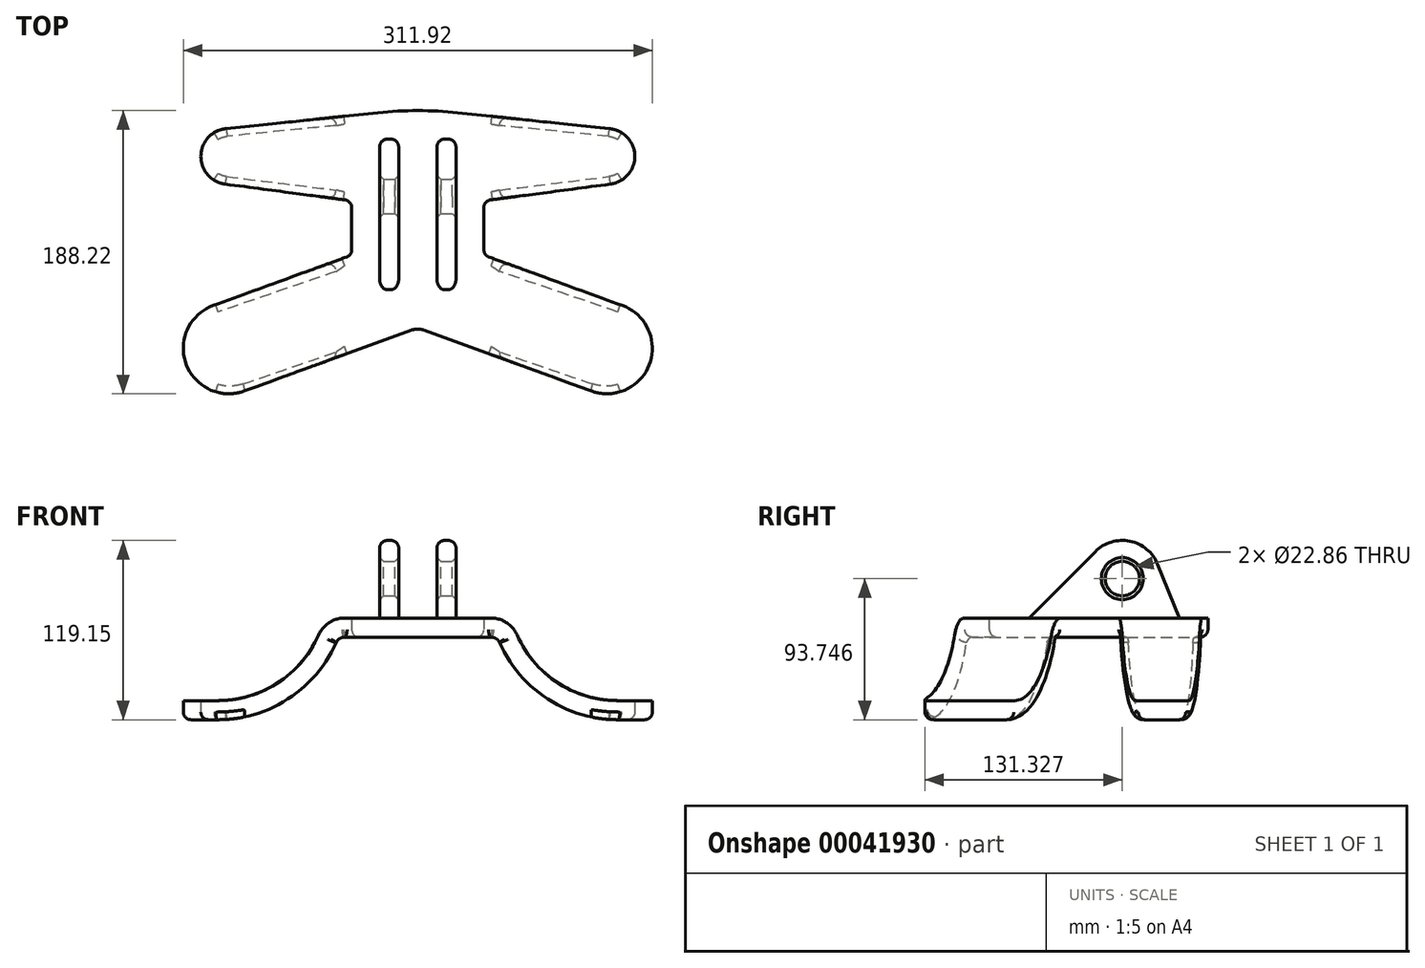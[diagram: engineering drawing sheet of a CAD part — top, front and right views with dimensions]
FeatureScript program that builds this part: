
annotation { "Feature Type Name" : "Feature", "Feature Type Description" : "" }
export const myFeature = defineFeature(function(context is Context, id is Id, definition is map)
    precondition{}
    {
        {
            var Q0;
            Q0=qCreatedBy(makeId("Top.planeOp"),FACE);
            var sketch = newSketch(context, id + "F0", { "sketchPlane" : qUnion([Q0])});
            skLineSegment(sketch, "E0", {"start": v(0, 0) * mm, "end": v(0, -145.8) * mm});
            skLineSegment(sketch, "E1", {"start": v(0, -145.8) * mm, "end": v(115.4, -187.8) * mm});
            skLineSegment(sketch, "E2", {"start": v(115.4, -187.8) * mm, "end": v(136.07, -130.99) * mm});
            skLineSegment(sketch, "E3", {"start": v(136.07, -130.99) * mm, "end": v(47.28, -98.67) * mm});
            skLineSegment(sketch, "E4", {"start": v(43.94, -93.9) * mm, "end": v(43.94, -65.78) * mm});
            skLineSegment(sketch, "E5", {"start": v(48.36, -60.75) * mm, "end": v(128.15, -50.24) * mm});
            skLineSegment(sketch, "E6", {"start": v(128.15, -50.24) * mm, "end": v(127.67, -13.42) * mm});
            skLineSegment(sketch, "E7", {"start": v(127.67, -13.42) * mm, "end": v(0, 0) * mm});
            skArc(sketch, "E8", {"start": v(128.15, -50.24) * mm, "mid": v(144.27, -31.62) * mm, "end": v(127.67, -13.42) * mm});
            skArc(sketch, "E9", {"start": v(115.4, -187.8) * mm, "mid": v(154.13, -169.73) * mm, "end": v(136.07, -130.99) * mm});
            skPoint(sketch, "E10.visualSharp", {"position": v(43.94, -61.33) * mm});
            skArc(sketch, "E10.filletArc", {"start": v(48.36, -60.75) * mm, "mid": v(45.2, -62.43) * mm, "end": v(43.94, -65.78) * mm});
            skPoint(sketch, "E11.visualSharp", {"position": v(43.94, -97.46) * mm});
            skArc(sketch, "E11.filletArc", {"start": v(43.94, -93.9) * mm, "mid": v(44.86, -96.81) * mm, "end": v(47.28, -98.67) * mm});
            skSolve(sketch);
        }
        {
            var Q0;
            Q0=makeQuery(id+"F0.imprint","IMPRINT",FACE,{"disambiguationData":[TD([[makeQuery(id+"F0.imprint","IMPRINT",EDGE,{"derivedFrom":sQuery(id+"F0.wireOp",EDGE,"E0")}),1.0]])]});
            var Q1;
            Q1=makeQuery(id+"F0.imprint","IMPRINT",FACE,{"disambiguationData":[TD([[makeQuery(id+"F0.imprint","IMPRINT",EDGE,{"derivedFrom":sQuery(id+"F0.wireOp",EDGE,"E6")}),-1.0]])]});
            var Q2;
            Q2=makeQuery(id+"F0.imprint","IMPRINT",FACE,{"disambiguationData":[TD([[makeQuery(id+"F0.imprint","IMPRINT",EDGE,{"derivedFrom":sQuery(id+"F0.wireOp",EDGE,"E2")}),-1.0]])]});
            extrude(context, id + "F1", {"entities" : qUnion([Q0, Q1, Q2]), "depth" : 76.2 * mm});
        }
        {
            var Q0;
            Q0=qCreatedBy(makeId("Front.planeOp"),FACE);
            var sketch = newSketch(context, id + "F2", { "sketchPlane" : qUnion([Q0])});
            skLineSegment(sketch, "E12", {"start": v(0, 61.21) * mm, "end": v(48.77, 61.21) * mm});
            skLineSegment(sketch, "E13", {"start": v(155.96, 6.35) * mm, "end": v(132.9, 6.35) * mm});
            skArc(sketch, "E14", {"start": v(54.35, 57.58) * mm, "mid": v(52.1, 60.22) * mm, "end": v(48.77, 61.21) * mm});
            skArc(sketch, "E15", {"start": v(54.35, 57.58) * mm, "mid": v(86.01, 20.29) * mm, "end": v(132.9, 6.35) * mm});
            skLineSegment(sketch, "E16.0", {"start": v(115.4, 0) * mm, "end": v(155.96, 0) * mm});
            skLineSegment(sketch, "E17.0", {"start": v(155.96, 19.05) * mm, "end": v(132.9, 19.05) * mm});
            skArc(sketch, "E17.1", {"start": v(65.97, 62.7) * mm, "mid": v(92.95, 30.93) * mm, "end": v(132.9, 19.05) * mm});
            skArc(sketch, "E17.2", {"start": v(48.77, 73.91) * mm, "mid": v(59.03, 70.86) * mm, "end": v(65.97, 62.7) * mm});
            skLineSegment(sketch, "E17.3", {"start": v(0, 73.91) * mm, "end": v(48.77, 73.91) * mm});
            skLineSegment(sketch, "E18", {"start": v(0, 73.91) * mm, "end": v(0, 101.24) * mm});
            skLineSegment(sketch, "E19", {"start": v(0, 101.24) * mm, "end": v(155.96, 101.24) * mm});
            skLineSegment(sketch, "E20", {"start": v(155.96, 101.24) * mm, "end": v(155.96, 19.05) * mm});
            skLineSegment(sketch, "E21", {"start": v(155.96, 6.35) * mm, "end": v(155.96, -17.55) * mm});
            skLineSegment(sketch, "E22", {"start": v(155.96, -17.55) * mm, "end": v(0, -17.55) * mm});
            skLineSegment(sketch, "E23", {"start": v(0, -17.55) * mm, "end": v(0, 61.21) * mm});
            skSolve(sketch);
        }
        {
            var Q0;
            {Q0=qUnion([makeQuery(id+"F2.imprint","IMPRINT",FACE,{"disambiguationData":[TD([[makeQuery(id+"F2.imprint","IMPRINT",EDGE,{"derivedFrom":sQuery(id+"F2.wireOp",EDGE,"E12")}),-1.0]])]}),makeQuery(id+"F2.imprint","IMPRINT",FACE,{"disambiguationData":[TD([[makeQuery(id+"F2.imprint","IMPRINT",EDGE,{"derivedFrom":sQuery(id+"F2.wireOp",EDGE,"E17.0")}),-1.0]])]})]);}
            extrude(context, id + "F3", {"entities" : qUnion([Q0]), "operationType" : NewBodyOperationType.REMOVE, "endBound" : BoundingType.THROUGH_ALL, "depth" : 230.42 * mm});
        }
        {
            var Q0;
            Q0=makeQuery(id+"F3.opExtrude","SWEPT_FACE",FACE,{"disambiguationData":[OSD([sQuery(id+"F2.wireOp",EDGE,"E17.3")])]});
            var sketch = newSketch(context, id + "F4", { "sketchPlane" : qUnion([Q0])});
            skArc(sketch, "E24.0", {"start": v(132.9, -14.76) * mm, "mid": v(144.27, -31.86) * mm, "end": v(132.9, -48.96) * mm});
            skArc(sketch, "E24.1", {"start": v(136.07, -130.99) * mm, "mid": v(155.91, -161.04) * mm, "end": v(132.9, -188.75) * mm});
            skCircle(sketch, "E25", {"center": v(125.73, -31.86) * mm, "radius": 9.53 * mm});
            skCircle(sketch, "E26", {"center": v(125.73, -159.4) * mm, "radius": 15.24 * mm});
            skSolve(sketch);
        }
        {
            var Q0;
            Q0=makeQuery(id+"F1.opExtrude","SWEPT_FACE",FACE,{"disambiguationData":[OSD([sQuery(id+"F0.wireOp",EDGE,"E0")])]});
            var sketch = newSketch(context, id + "F5", { "sketchPlane" : qUnion([Q0])});
            skLineSegment(sketch, "E27", {"start": v(20.32, 73.91) * mm, "end": v(120.4, 73.91) * mm});
            skLineSegment(sketch, "E28", {"start": v(120.4, 73.91) * mm, "end": v(76.25, 118.06) * mm});
            skLineSegment(sketch, "E29", {"start": v(34.74, 109.61) * mm, "end": v(20.32, 73.91) * mm});
            skArc(sketch, "E30", {"start": v(76.25, 118.06) * mm, "mid": v(53.23, 124.99) * mm, "end": v(34.74, 109.61) * mm});
            skSolve(sketch);
        }
        {
            var Q0;
            Q0=makeQuery(id+"F5.imprint","IMPRINT",FACE,{"disambiguationData":[TD([[makeQuery(id+"F5.imprint","IMPRINT",EDGE,{"derivedFrom":sQuery(id+"F5.wireOp",EDGE,"E27")}),-1.0]])]});
            extrude(context, id + "F6", {"entities" : qUnion([Q0]), "operationType" : NewBodyOperationType.ADD, "oppositeDirection" : true, "depth" : 25.4 * mm});
        }
        {
            var Q0;
            Q0=makeQuery(id+"F1.opExtrude","SWEPT_BODY",BODY,{"disambiguationData":[OSD([sQuery(id+"F0.wireOp",EDGE,"E0"),sQuery(id+"F0.wireOp",EDGE,"E1"),sQuery(id+"F0.wireOp",EDGE,"E3"),sQuery(id+"F0.wireOp",EDGE,"E4"),sQuery(id+"F0.wireOp",EDGE,"E5"),sQuery(id+"F0.wireOp",EDGE,"E7"),sQuery(id+"F0.wireOp",EDGE,"E8"),sQuery(id+"F0.wireOp",EDGE,"E9"),sQuery(id+"F0.wireOp",EDGE,"E10.filletArc"),sQuery(id+"F0.wireOp",EDGE,"E11.filletArc")])]});
            var Q1;
            Q1=makeQuery(id+"F6.boolean.opBoolean","MERGE",FACE,{"derivedFrom":[makeQuery(id+"F1.opExtrude","SWEPT_FACE",FACE,{"disambiguationData":[OSD([sQuery(id+"F0.wireOp",EDGE,"E0")])]}),makeQuery(id+"F6.opExtrude","CAP_FACE",FACE,{"disambiguationData":[OSD([sQuery(id+"F5.wireOp",EDGE,"E27"),sQuery(id+"F5.wireOp",EDGE,"E28"),sQuery(id+"F5.wireOp",EDGE,"E29"),sQuery(id+"F5.wireOp",EDGE,"E30")])],"isStart":true})]});
            mirror(context, id + "F7", {"entities" : qUnion([Q0]), "mirrorPlane" : qUnion([Q1])});
        }
        {
            var Q0;
            Q0=makeQuery(id+"F7.opPattern","COPY",BODY,{"derivedFrom":makeQuery(id+"F1.opExtrude","SWEPT_BODY",BODY,{"disambiguationData":[OSD([sQuery(id+"F0.wireOp",EDGE,"E0"),sQuery(id+"F0.wireOp",EDGE,"E1"),sQuery(id+"F0.wireOp",EDGE,"E3"),sQuery(id+"F0.wireOp",EDGE,"E4"),sQuery(id+"F0.wireOp",EDGE,"E5"),sQuery(id+"F0.wireOp",EDGE,"E7"),sQuery(id+"F0.wireOp",EDGE,"E8"),sQuery(id+"F0.wireOp",EDGE,"E9"),sQuery(id+"F0.wireOp",EDGE,"E10.filletArc"),sQuery(id+"F0.wireOp",EDGE,"E11.filletArc")])]}),"instanceName":"1"});
            var Q1;
            Q1=makeQuery(id+"F1.opExtrude","SWEPT_BODY",BODY,{"disambiguationData":[OSD([sQuery(id+"F0.wireOp",EDGE,"E0"),sQuery(id+"F0.wireOp",EDGE,"E1"),sQuery(id+"F0.wireOp",EDGE,"E3"),sQuery(id+"F0.wireOp",EDGE,"E4"),sQuery(id+"F0.wireOp",EDGE,"E5"),sQuery(id+"F0.wireOp",EDGE,"E7"),sQuery(id+"F0.wireOp",EDGE,"E8"),sQuery(id+"F0.wireOp",EDGE,"E9"),sQuery(id+"F0.wireOp",EDGE,"E10.filletArc"),sQuery(id+"F0.wireOp",EDGE,"E11.filletArc")])]});
            booleanBodies(context, id + "F8", {"operationType" : BooleanOperationType.UNION, "tools" : qUnion([Q0, Q1])});
        }
        {
            var Q0;
            {var subQ0=makeQuery(id+"F1.opExtrude","SWEPT_EDGE",EDGE,{"disambiguationData":[OSD([sQuery(id+"F0.wireOp",EDGE,"E0"),sQuery(id+"F0.wireOp",EDGE,"E7")])]});Q0=makeQuery(id+"F8.opBoolean","MERGE",EDGE,{"derivedFrom":[subQ0,makeQuery(id+"F7.opPattern","COPY",EDGE,{"derivedFrom":subQ0,"instanceName":"1"})]});}
            fillet(context, id + "F9", {"entities" : qUnion([Q0]), "radius" : 254 * mm, "tangentPropagation" : true, "allowEdgeOverflow" : false});
        }
        {
            var Q0;
            Q0=qCreatedBy(makeId("Front.planeOp"),FACE);
            cPlane(context, id + "F10", {"entities" : qUnion([Q0]), "cplaneType" : CPlaneType.OFFSET, "offset" : 152.4 * mm, "width" : 152.4 * mm, "height" : 152.4 * mm});
        }
        {
            var Q0;
            Q0=qCreatedBy(id+"F10.planeOp",FACE);
            var sketch = newSketch(context, id + "F11", { "sketchPlane" : qUnion([Q0])});
            skLineSegment(sketch, "E31.rect.bottom", {"start": v(12.7, 73.91) * mm, "end": v(-12.7, 73.91) * mm});
            skLineSegment(sketch, "E31.rect.top", {"start": v(12.7, 137.41) * mm, "end": v(-12.7, 137.41) * mm});
            skLineSegment(sketch, "E31.rect.left", {"start": v(12.7, 73.91) * mm, "end": v(12.7, 137.41) * mm});
            skLineSegment(sketch, "E31.rect.right", {"start": v(-12.7, 73.91) * mm, "end": v(-12.7, 137.41) * mm});
            skPoint(sketch, "E31.rect.middle", {"position": v(0, 105.66) * mm});
            skSolve(sketch);
        }
        {
            var Q0;
            Q0=makeQuery(id+"F11.imprint","IMPRINT",FACE,{"disambiguationData":[TD([[makeQuery(id+"F11.imprint","IMPRINT",EDGE,{"derivedFrom":sQuery(id+"F11.wireOp",EDGE,"E31.rect.bottom")}),-1.0]])]});
            extrude(context, id + "F12", {"entities" : qUnion([Q0]), "operationType" : NewBodyOperationType.REMOVE, "endBound" : BoundingType.THROUGH_ALL, "oppositeDirection" : true, "depth" : 25.4 * mm});
        }
        {
            var Q0;
            Q0=makeQuery(id+"F6.opExtrude","CAP_FACE",FACE,{"disambiguationData":[OSD([sQuery(id+"F5.wireOp",EDGE,"E27"),sQuery(id+"F5.wireOp",EDGE,"E28"),sQuery(id+"F5.wireOp",EDGE,"E29"),sQuery(id+"F5.wireOp",EDGE,"E30")])],"isStart":false});
            var sketch = newSketch(context, id + "F13", { "sketchPlane" : qUnion([Q0])});
            skArc(sketch, "E32.0", {"start": v(-76.25, 118.06) * mm, "mid": v(-53.23, 124.99) * mm, "end": v(-34.74, 109.61) * mm});
            skCircle(sketch, "E33", {"center": v(-58.3, 100.1) * mm, "radius": 11.43 * mm});
            skSolve(sketch);
        }
        {
            var Q0;
            Q0=makeQuery(id+"F13.imprint","IMPRINT",FACE,{"disambiguationData":[TD([[makeQuery(id+"F13.imprint","IMPRINT",EDGE,{"derivedFrom":sQuery(id+"F13.wireOp",EDGE,"E33")}),1.0]])]});
            extrude(context, id + "F14", {"entities" : qUnion([Q0]), "operationType" : NewBodyOperationType.REMOVE, "endBound" : BoundingType.THROUGH_ALL, "oppositeDirection" : true, "depth" : 25.4 * mm});
        }
        {
            var Q0;
            {var subQ0=makeQuery(id+"F1.opExtrude","SWEPT_EDGE",EDGE,{"disambiguationData":[OSD([sQuery(id+"F0.wireOp",EDGE,"E0"),sQuery(id+"F0.wireOp",EDGE,"E1")])]});Q0=makeQuery(id+"F8.opBoolean","MERGE",EDGE,{"derivedFrom":[subQ0,makeQuery(id+"F7.opPattern","COPY",EDGE,{"derivedFrom":subQ0,"instanceName":"1"})]});}
            fillet(context, id + "F15", {"entities" : qUnion([Q0]), "radius" : 12.7 * mm, "tangentPropagation" : true, "allowEdgeOverflow" : false});
        }
        {
            var Q0;
            {var subQ0=makeQuery(id+"F1.opExtrude","SWEPT_EDGE",EDGE,{"disambiguationData":[OSD([sQuery(id+"F0.wireOp",EDGE,"E0"),sQuery(id+"F0.wireOp",EDGE,"E1")])]});var subQ1=makeQuery(id+"F3.opExtrude","SWEPT_FACE",FACE,{"disambiguationData":[OSD([sQuery(id+"F2.wireOp",EDGE,"E17.3")])]});Q0=makeQuery(id+"F15.opFillet","BLEND_EDGE",EDGE,{"blendedFrom":[makeQuery(id+"F8.opBoolean","MERGE",EDGE,{"derivedFrom":[subQ0,makeQuery(id+"F7.opPattern","COPY",EDGE,{"derivedFrom":subQ0,"instanceName":"1"})]}),makeQuery(id+"F12.boolean.opBoolean","MERGE",FACE,{"derivedFrom":[makeQuery(id+"F8.opBoolean","MERGE",FACE,{"derivedFrom":[subQ1,makeQuery(id+"F7.opPattern","COPY",FACE,{"derivedFrom":subQ1,"instanceName":"1"})]}),makeQuery(id+"F12.opExtrude","SWEPT_FACE",FACE,{"disambiguationData":[OSD([sQuery(id+"F11.wireOp",EDGE,"E31.rect.bottom")])]})]})],"blendedInto":[makeQuery(id+"F12.boolean.opBoolean","MERGE",FACE,{"derivedFrom":[makeQuery(id+"F8.opBoolean","MERGE",FACE,{"derivedFrom":[subQ1,makeQuery(id+"F7.opPattern","COPY",FACE,{"derivedFrom":subQ1,"instanceName":"1"})]}),makeQuery(id+"F12.opExtrude","SWEPT_FACE",FACE,{"disambiguationData":[OSD([sQuery(id+"F11.wireOp",EDGE,"E31.rect.bottom")])]})]})]});}
            var Q1;
            Q1=makeQuery(id+"F7.opPattern","COPY",EDGE,{"derivedFrom":makeQuery(id+"F3.boolean.opBoolean","INTERSECT",EDGE,{"derivedFrom":[makeQuery(id+"F1.opExtrude","SWEPT_FACE",FACE,{"disambiguationData":[OSD([sQuery(id+"F0.wireOp",EDGE,"E1")])]}),makeQuery(id+"F3.opExtrude","SWEPT_FACE",FACE,{"disambiguationData":[OSD([sQuery(id+"F2.wireOp",EDGE,"E12")])]})]}),"instanceName":"1"});
            var Q2;
            {var subQ0=makeQuery(id+"F3.opExtrude","SWEPT_FACE",FACE,{"disambiguationData":[OSD([sQuery(id+"F2.wireOp",EDGE,"E17.3")])]});Q2=makeQuery(id+"F12.boolean.opBoolean","MERGE",FACE,{"derivedFrom":[makeQuery(id+"F8.opBoolean","MERGE",FACE,{"derivedFrom":[subQ0,makeQuery(id+"F7.opPattern","COPY",FACE,{"derivedFrom":subQ0,"instanceName":"1"})]}),makeQuery(id+"F12.opExtrude","SWEPT_FACE",FACE,{"disambiguationData":[OSD([sQuery(id+"F11.wireOp",EDGE,"E31.rect.bottom")])]})]});}
            var Q3;
            {var subQ0=makeQuery(id+"F6.opExtrude","SWEPT_FACE",FACE,{"disambiguationData":[OSD([sQuery(id+"F5.wireOp",EDGE,"E28")])]});Q3=makeQuery(id+"F12.boolean.opBoolean","INTERSECT",EDGE,{"derivedFrom":[makeQuery(id+"F8.opBoolean","MERGE",FACE,{"derivedFrom":[subQ0,makeQuery(id+"F7.opPattern","COPY",FACE,{"derivedFrom":subQ0,"instanceName":"1"})]}),makeQuery(id+"F12.opExtrude","SWEPT_FACE",FACE,{"disambiguationData":[OSD([sQuery(id+"F11.wireOp",EDGE,"E31.rect.right")])]})]});}
            var Q4;
            Q4=makeQuery(id+"F7.opPattern","COPY",EDGE,{"derivedFrom":makeQuery(id+"F6.opExtrude","CAP_EDGE",EDGE,{"disambiguationData":[OSD([sQuery(id+"F5.wireOp",EDGE,"E28")])],"isStart":false}),"instanceName":"1"});
            var Q5;
            Q5=makeQuery(id+"F6.opExtrude","CAP_EDGE",EDGE,{"disambiguationData":[OSD([sQuery(id+"F5.wireOp",EDGE,"E28")])],"isStart":false});
            var Q6;
            {var subQ0=makeQuery(id+"F6.opExtrude","SWEPT_FACE",FACE,{"disambiguationData":[OSD([sQuery(id+"F5.wireOp",EDGE,"E28")])]});Q6=makeQuery(id+"F12.boolean.opBoolean","INTERSECT",EDGE,{"derivedFrom":[makeQuery(id+"F8.opBoolean","MERGE",FACE,{"derivedFrom":[subQ0,makeQuery(id+"F7.opPattern","COPY",FACE,{"derivedFrom":subQ0,"instanceName":"1"})]}),makeQuery(id+"F12.opExtrude","SWEPT_FACE",FACE,{"disambiguationData":[OSD([sQuery(id+"F11.wireOp",EDGE,"E31.rect.left")])]})]});}
            fillet(context, id + "F16", {"entities" : qUnion([Q0, Q1, Q2, Q3, Q4, Q5, Q6]), "radius" : 5.08 * mm, "tangentPropagation" : true, "allowEdgeOverflow" : false});
        }
        {
            var Q0;
            Q0=makeQuery(id+"F14.boolean.opBoolean","COPY",FACE,{"disambiguationData":[OD(0.0)],"derivedFrom":makeQuery(id+"F14.opExtrude","SWEPT_FACE",FACE,{"disambiguationData":[OSD([sQuery(id+"F13.wireOp",EDGE,"E33")])]})});
            var Q1;
            Q1=makeQuery(id+"F14.boolean.opBoolean","COPY",FACE,{"disambiguationData":[OD(1.0)],"derivedFrom":makeQuery(id+"F14.opExtrude","SWEPT_FACE",FACE,{"disambiguationData":[OSD([sQuery(id+"F13.wireOp",EDGE,"E33")])]})});
            chamfer(context, id + "F17", {"entities" : qUnion([Q0, Q1]), "width" : 2.54 * mm, "tangentPropagation" : true});
        }
    });
